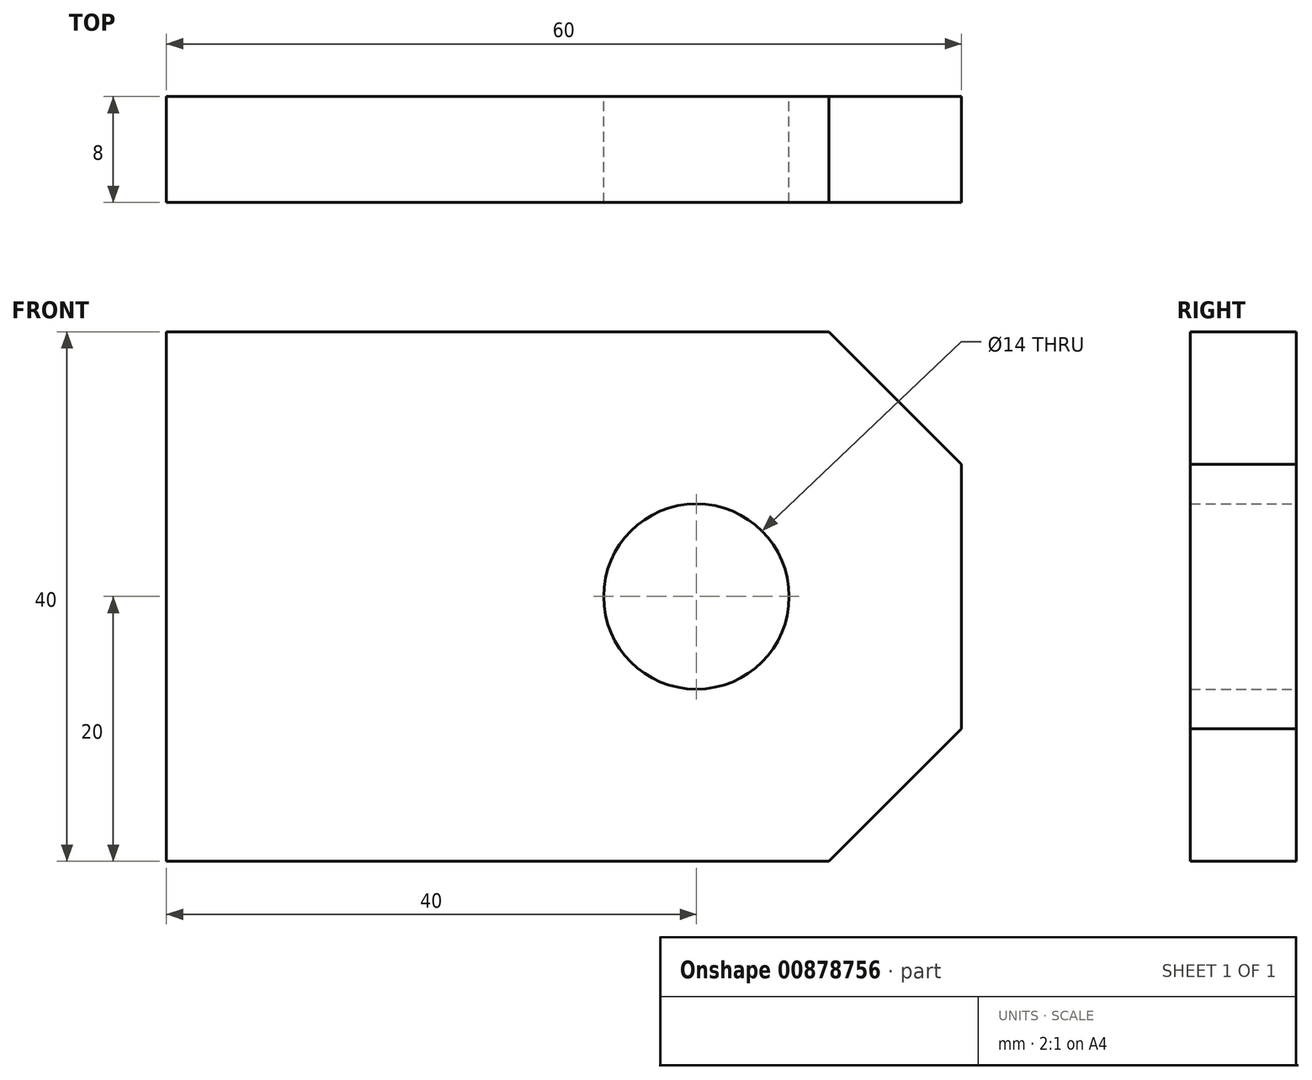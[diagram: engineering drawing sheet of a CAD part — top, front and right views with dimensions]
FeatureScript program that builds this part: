
annotation { "Feature Type Name" : "Feature", "Feature Type Description" : "" }
export const myFeature = defineFeature(function(context is Context, id is Id, definition is map)
    precondition{}
    {
        {
            var Q0;
            Q0=qCreatedBy(makeId("Front.planeOp"),FACE);
            var sketch = newSketch(context, id + "F0", { "sketchPlane" : qUnion([Q0])});
            skLineSegment(sketch, "E0.bottom", {"start": v(-30, 20) * mm, "end": v(30, 20) * mm});
            skLineSegment(sketch, "E0.top", {"start": v(-30, -20) * mm, "end": v(30, -20) * mm});
            skLineSegment(sketch, "E0.left", {"start": v(-30, 20) * mm, "end": v(-30, -20) * mm});
            skLineSegment(sketch, "E0.right", {"start": v(30, 20) * mm, "end": v(30, -20) * mm});
            skPoint(sketch, "E0.middle", {"position": v(0, 0) * mm});
            skCircle(sketch, "E1", {"center": v(10, 0) * mm, "radius": 7 * mm});
            skSolve(sketch);
        }
        {
            var Q0;
            Q0=makeQuery(id+"F0.imprint","IMPRINT",FACE,{"disambiguationData":[TD([[makeQuery(id+"F0.imprint","IMPRINT",EDGE,{"derivedFrom":sQuery(id+"F0.wireOp",EDGE,"E0.bottom")}),-1.0]])]});
            extrude(context, id + "F1", {"entities" : qUnion([Q0]), "depth" : 8 * mm, "offsetDistance" : 25 * mm});
        }
        {
            var Q0;
            Q0=makeQuery(id+"F1.opExtrude","SWEPT_EDGE",EDGE,{"disambiguationData":[OSD([sQuery(id+"F0.wireOp",EDGE,"E0.top"),sQuery(id+"F0.wireOp",EDGE,"E0.right")])]});
            var Q1;
            Q1=makeQuery(id+"F1.opExtrude","SWEPT_EDGE",EDGE,{"disambiguationData":[OSD([sQuery(id+"F0.wireOp",EDGE,"E0.bottom"),sQuery(id+"F0.wireOp",EDGE,"E0.right")])]});
            chamfer(context, id + "F2", {"entities" : qUnion([Q0, Q1]), "width" : 10 * mm, "tangentPropagation" : true});
        }
    });
